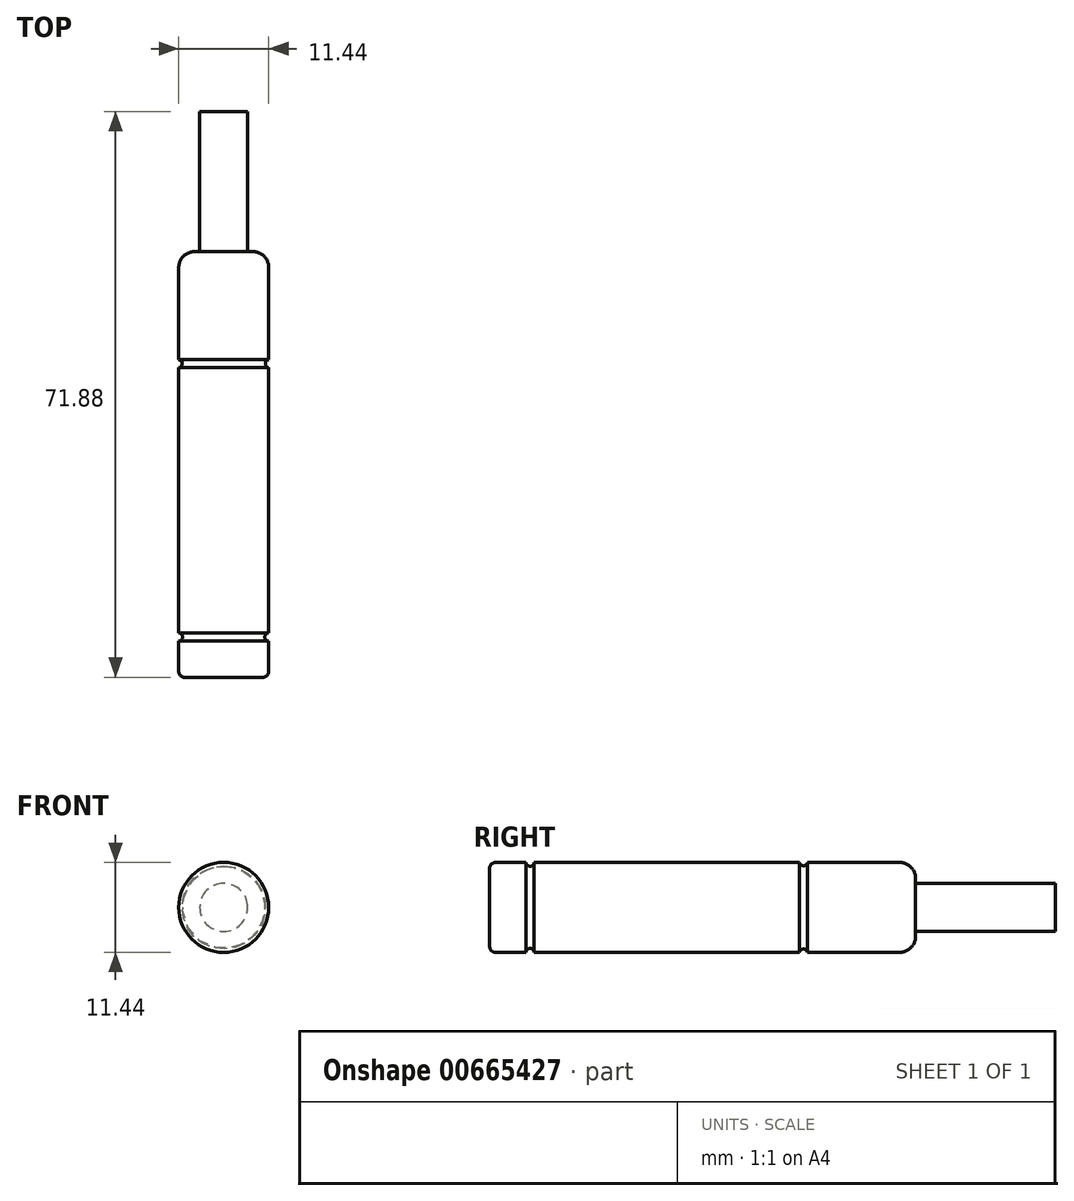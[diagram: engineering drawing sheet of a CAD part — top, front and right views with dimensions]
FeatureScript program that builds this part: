
annotation { "Feature Type Name" : "Feature", "Feature Type Description" : "" }
export const myFeature = defineFeature(function(context is Context, id is Id, definition is map)
    precondition{}
    {
        {
            var Q0;
            Q0=qCreatedBy(makeId("Front.planeOp"),FACE);
            var sketch = newSketch(context, id + "F0", { "sketchPlane" : qUnion([Q0])});
            skCircle(sketch, "E0", {"center": v(0, 0) * mm, "radius": 5.72 * mm});
            skSolve(sketch);
        }
        {
            var Q0;
            Q0=makeQuery(id+"F0.imprint","IMPRINT",FACE,{"disambiguationData":[TD([[makeQuery(id+"F0.imprint","IMPRINT",EDGE,{"derivedFrom":sQuery(id+"F0.wireOp",EDGE,"E0")}),1.0]])]});
            var Q1;
            Q1=sQuery(id+"F0.wireOp",EDGE,"E0");
            extrude(context, id + "F1", {"entities" : qUnion([Q0]), "surfaceEntities" : qUnion([Q1]), "depth" : 54.1 * mm, "offsetDistance" : 25.4 * mm});
        }
        {
            var Q0;
            Q0=qCreatedBy(makeId("Front.planeOp"),FACE);
            var sketch = newSketch(context, id + "F2", { "sketchPlane" : qUnion([Q0])});
            skCircle(sketch, "E1", {"center": v(0, 0) * mm, "radius": 3.05 * mm});
            skSolve(sketch);
        }
        {
            var Q0;
            Q0=makeQuery(id+"F2.imprint","IMPRINT",FACE,{"disambiguationData":[TD([[makeQuery(id+"F2.imprint","IMPRINT",EDGE,{"derivedFrom":sQuery(id+"F2.wireOp",EDGE,"E1")}),1.0]])]});
            extrude(context, id + "F3", {"entities" : qUnion([Q0]), "operationType" : NewBodyOperationType.ADD, "depth" : -17.78 * mm, "offsetDistance" : 25.4 * mm});
        }
        {
            var Q0;
            Q0=makeQuery(id+"F1.opExtrude","CAP_EDGE",EDGE,{"disambiguationData":[OSD([sQuery(id+"F0.wireOp",EDGE,"E0")])],"isStart":true});
            fillet(context, id + "F4", {"entities" : qUnion([Q0]), "radius" : 2.03 * mm, "tangentPropagation" : true, "allowEdgeOverflow" : false});
        }
        {
            var Q0;
            Q0=makeQuery(id+"F1.opExtrude","CAP_EDGE",EDGE,{"disambiguationData":[OSD([sQuery(id+"F0.wireOp",EDGE,"E0")])],"isStart":false});
            fillet(context, id + "F5", {"entities" : qUnion([Q0]), "radius" : 0.76 * mm, "tangentPropagation" : true, "allowEdgeOverflow" : false});
        }
        {
            var Q0;
            Q0=qCreatedBy(makeId("Top.planeOp"),FACE);
            var sketch = newSketch(context, id + "F6", { "sketchPlane" : qUnion([Q0])});
            skCircle(sketch, "E2", {"center": v(5.74, -48.96) * mm, "radius": 0.52 * mm});
            skCircle(sketch, "E3", {"center": v(5.81, -14.24) * mm, "radius": 0.52 * mm});
            skLineSegment(sketch, "E4", {"start": v(0, -43.88) * mm, "end": v(0, -29.1) * mm});
            skSolve(sketch);
        }
        {
            var Q0;
            Q0=makeQuery(id+"F6.imprint","IMPRINT",FACE,{"disambiguationData":[TD([[makeQuery(id+"F6.imprint","IMPRINT",EDGE,{"derivedFrom":sQuery(id+"F6.wireOp",EDGE,"E2")}),1.0]])]});
            var Q1;
            Q1=makeQuery(id+"F6.imprint","IMPRINT",FACE,{"disambiguationData":[TD([[makeQuery(id+"F6.imprint","IMPRINT",EDGE,{"derivedFrom":sQuery(id+"F6.wireOp",EDGE,"E3")}),1.0]])]});
            var Q2;
            Q2=sQuery(id+"F6.wireOp",EDGE,"E4");
            revolve(context, id + "F7", {"operationType" : NewBodyOperationType.REMOVE, "entities" : qUnion([Q0, Q1]), "axis" : qUnion([Q2]), "revolveType" : RevolveType.FULL, "oppositeDirection" : true});
        }
    });
